# Revit family: IS_Connect_Multiproduct_BIM_IT_E0483;E0493
name_source: partatom
category: Plumbing Fixtures
revit_build: Autodesk Revit MEP 2014 (Build: 20130308_1515(x64)
units: mm (PartAtom-declared; Revit-internal decimal feet)

## types (2) — shared parameters
Accessori = www.idealstandard.it
AltezzaNominale = 339 mm
Assembly Code = C1030200
Autore = Ideal Standard Italia
Brand = Ideal Standard
Caratteristiche = Vaso sospeso AquaBlade® con fissaggi completamente nascosti, completo di sedile slim a sgancio rapido.  La tecnologia AquaBlade® crea una lama d’acqua che pulisce una superficie più ampia del 90% rispetto a un vaso con brida. Grazie al design innovativo inoltre elimina gli angoli nascosti rendendo comodamente accessibile l’intera superficie del vaso per una pulizia più efficace. Per il fissaggio a parete è necessario utilizzare l’apposito kit TT0299327 incluso nella confezione ed il sostegno metallico T655067 da ordinare separatamente. Certificato per scarico 4,5/3 litri.
Colore = Bianco
Connessione = Installazione
DescrizioneClassifcazioneUni2015 = WC pans
Dimensione = 340 x 545 x 363 mm
DurataGaranziaProdotti = 99
Finitura = Bianco
Garanzia = Garanzia Idealstandard
IfcEsportaCome = IfcSanitaryTerminalType
InformaziniGaranzia = www.idealstandard.it/garanzia.html
InformazioniDiProdotto = www.idealstandard.it/prodotti/html
InformazioniGaranzia = www.idealstandard.it/garanzia.html
InstruzioniInstallazione = www.idealstandard.it/prodotti/html
LarghezzaNominale = 362 mm
LunghezzaNominale = 545 mm  [stored 1.78806 ft]
Materiale = Porcellana Vetrificata (Vitreous China)
NBSDescription = WC pans
NBSReference = 45-30-70/384
PesoNetto = 22,00 KG
Produttore = www.idealstandard.it
ProfonditàNominale = 545 mm  [stored 1.78806 ft]
Revisione = 1
RiferimentoClassificazioneUni2015 = Pr_40_20_93_94
Spazio = interno
Telefono = 800 652 290
TipoEspotazioneIfc = WCPANS
URL = www.idealstandard.it
UnitàDurata = anni
UnitàDurataGaranzia = anni
UnitàVolume = Litri
VersioneClassificazioneUni2015 = Products v1.1
zero-valued in all types: CWFU, Cost, CostoDiSostituzione, Default Elevation, HWFU, SpilloverLivello, WFU

## per-type parameters (varying)
| type | CodiceABarre | Description | E772301 | E772401 | Model | Nome | NomeOggettoBim | NumeroDiModello |
| E048301 - CONNECT WH BOWL AB NC THIN HF RS WHITE | 5017830501589 | CONNECT WH BOWL AB NC THIN HF RS WHITE | Yes | No | E048301 | WcPans_CONNECT_E048301_IdealStandard | ISI_IdealStandard_WcPans_CONNECT_E048301 | E048301 |
| E049301 - CONNECT WH BOWL AB SC THIN HF RS WHITE | 5017830501596 | CONNECT WH BOWL AB SC THIN HF RS WHITE | No | Yes | E049301 | WcPans_CONNECT_E049301_IdealStandard | ISI_IdealStandard_WcPans_CONNECT_E049301 | E049301 |

note: [stored X ft] marks values corroborated as IEEE doubles in the binary element streams (Revit-internal decimal feet)

## geometry (parser evidence)
native form markers: Sweep x8
no freeform markers — native parametric forms only
